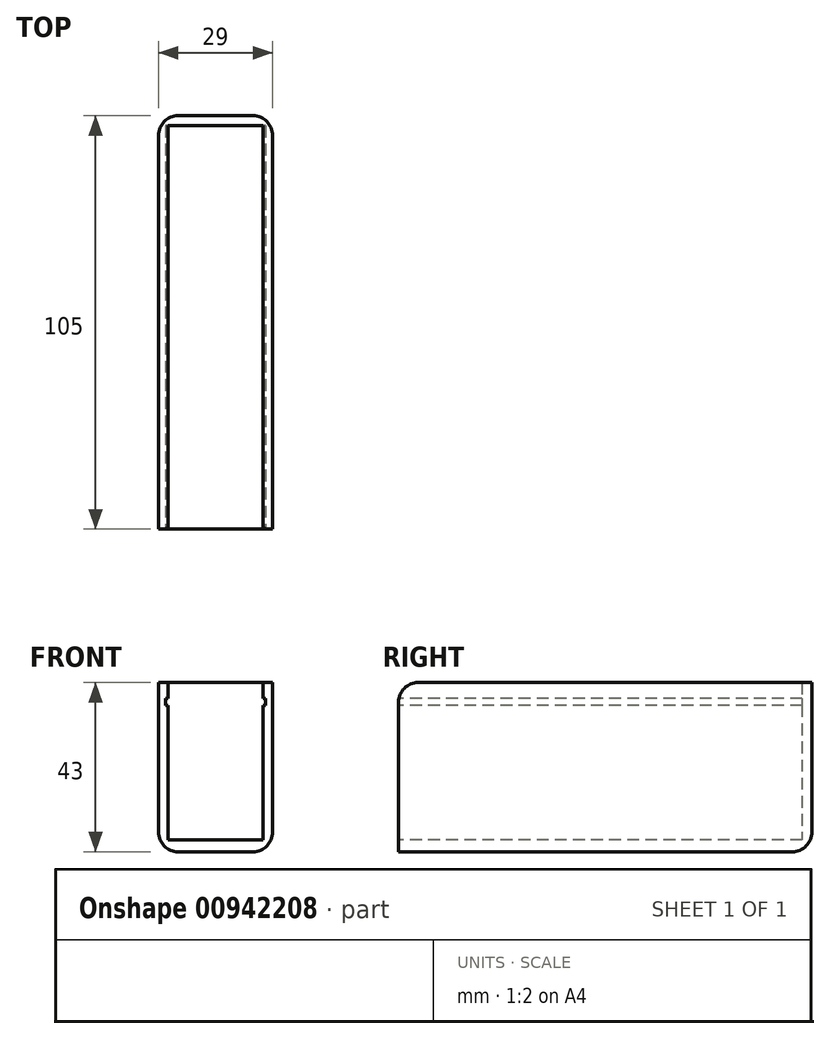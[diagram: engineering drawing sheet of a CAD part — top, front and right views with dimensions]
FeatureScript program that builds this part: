
annotation { "Feature Type Name" : "Feature", "Feature Type Description" : "" }
export const myFeature = defineFeature(function(context is Context, id is Id, definition is map)
    precondition{}
    {
        {
            var Q0;
            Q0=qCreatedBy(makeId("Top.planeOp"),FACE);
            var sketch = newSketch(context, id + "F0", { "sketchPlane" : qUnion([Q0])});
            skLineSegment(sketch, "E0.bottom", {"start": v(12, -50) * mm, "end": v(-12, -50) * mm});
            skLineSegment(sketch, "E0.top", {"start": v(12, 50) * mm, "end": v(-12, 50) * mm});
            skLineSegment(sketch, "E0.left", {"start": v(12, -50) * mm, "end": v(12, 50) * mm});
            skLineSegment(sketch, "E0.right", {"start": v(-12, -50) * mm, "end": v(-12, 50) * mm});
            skPoint(sketch, "E0.middle", {"position": v(0, 0) * mm});
            skLineSegment(sketch, "E1.bottom", {"start": v(14.5, -52.5) * mm, "end": v(-14.5, -52.5) * mm});
            skLineSegment(sketch, "E1.top", {"start": v(14.5, 52.5) * mm, "end": v(-14.5, 52.5) * mm});
            skLineSegment(sketch, "E1.left", {"start": v(14.5, -52.5) * mm, "end": v(14.5, 52.5) * mm});
            skLineSegment(sketch, "E1.right", {"start": v(-14.5, -52.5) * mm, "end": v(-14.5, 52.5) * mm});
            skLineSegment(sketch, "E2", {"start": v(-12, -50) * mm, "end": v(-12, -52.5) * mm});
            skLineSegment(sketch, "E3", {"start": v(12, -50) * mm, "end": v(12, -52.5) * mm});
            skSolve(sketch);
        }
        {
            var Q0;
            Q0=makeQuery(id+"F0.imprint","IMPRINT",FACE,{"disambiguationData":[TD([[makeQuery(id+"F0.imprint","IMPRINT",EDGE,{"derivedFrom":sQuery(id+"F0.wireOp",EDGE,"E0.top")}),-1.0]])]});
            extrude(context, id + "F1", {"entities" : qUnion([Q0]), "depth" : 40 * mm, "offsetDistance" : 25 * mm});
        }
        {
            var Q0;
            Q0=makeQuery(id+"F0.imprint","IMPRINT",FACE,{"disambiguationData":[TD([[makeQuery(id+"F0.imprint","IMPRINT",EDGE,{"derivedFrom":sQuery(id+"F0.wireOp",EDGE,"E0.bottom")}),-1.0]])]});
            var Q1;
            Q1=makeQuery(id+"F0.imprint","IMPRINT",FACE,{"disambiguationData":[TD([[makeQuery(id+"F0.imprint","IMPRINT",EDGE,{"derivedFrom":sQuery(id+"F0.wireOp",EDGE,"E0.top")}),-1.0]])]});
            var Q2;
            Q2=makeQuery(id+"F0.imprint","IMPRINT",FACE,{"disambiguationData":[TD([[makeQuery(id+"F0.imprint","IMPRINT",EDGE,{"derivedFrom":sQuery(id+"F0.wireOp",EDGE,"E0.bottom")}),1.0]])]});
            extrude(context, id + "F2", {"entities" : qUnion([Q0, Q1, Q2]), "operationType" : NewBodyOperationType.ADD, "oppositeDirection" : true, "depth" : 3 * mm, "offsetDistance" : 25 * mm});
        }
        {
            var Q0;
            {var subQ0=sQuery(id+"F0.wireOp",EDGE,"E1.bottom");Q0=makeQuery(id+"F2.boolean.opBoolean","MERGE",FACE,{"derivedFrom":[makeQuery(id+"F1.opExtrude","SWEPT_FACE",FACE,{"disambiguationData":[OSD([subQ0]),TDD([makeQuery(id+"F0.imprint","IMPRINT",EDGE,{"disambiguationData":[TD([[makeQuery(id+"F0.imprint","INTERSECT",VERTEX,{"derivedFrom":[subQ0,sQuery(id+"F0.wireOp",EDGE,"E1.left")]}),-1.0]])],"derivedFrom":subQ0})])]}),makeQuery(id+"F1.opExtrude","SWEPT_FACE",FACE,{"disambiguationData":[OSD([subQ0]),TDD([makeQuery(id+"F0.imprint","IMPRINT",EDGE,{"disambiguationData":[TD([[makeQuery(id+"F0.imprint","INTERSECT",VERTEX,{"derivedFrom":[subQ0,sQuery(id+"F0.wireOp",EDGE,"E1.right")]}),1.0]])],"derivedFrom":subQ0})])]}),makeQuery(id+"F2.opExtrude","SWEPT_FACE",FACE,{"disambiguationData":[OSD([subQ0])]})]});}
            var sketch = newSketch(context, id + "F3", { "sketchPlane" : qUnion([Q0])});
            skLineSegment(sketch, "E4", {"start": v(-12, 36) * mm, "end": v(-12.7, 36) * mm});
            skLineSegment(sketch, "E5", {"start": v(-12.7, 36) * mm, "end": v(-12.7, 34.2) * mm});
            skLineSegment(sketch, "E6", {"start": v(-12.7, 34.2) * mm, "end": v(-12, 34.2) * mm});
            skLineSegment(sketch, "E7.MirrorCS", {"start": v(12.7, 34.2) * mm, "end": v(12, 34.2) * mm});
            skLineSegment(sketch, "E8.MirrorCS", {"start": v(12, 36) * mm, "end": v(12.7, 36) * mm});
            skLineSegment(sketch, "E9.MirrorCS", {"start": v(12.7, 36) * mm, "end": v(12.7, 34.2) * mm});
            skSolve(sketch);
        }
        {
            var Q0;
            {var subQ0=sQuery(id+"F3.wireOp",EDGE,"E4");Q0=makeQuery(id+"F3.imprint","IMPRINT",FACE,{"disambiguationData":[TD([[makeQuery(id+"F3.imprint","IMPRINT",EDGE,{"derivedFrom":subQ0}),1.0]])]});}
            var Q1;
            {var subQ0=sQuery(id+"F3.wireOp",EDGE,"E7.MirrorCS");Q1=makeQuery(id+"F3.imprint","IMPRINT",FACE,{"disambiguationData":[TD([[makeQuery(id+"F3.imprint","IMPRINT",EDGE,{"derivedFrom":subQ0}),-1.0]])]});}
            extrude(context, id + "F4", {"entities" : qUnion([Q0, Q1]), "operationType" : NewBodyOperationType.REMOVE, "oppositeDirection" : true, "depth" : 102.5 * mm, "offsetDistance" : 25 * mm});
        }
        {
            var Q0;
            {var subQ0=sQuery(id+"F0.wireOp",EDGE,"E1.bottom");Q0=makeQuery(id+"F1.opExtrude","CAP_EDGE",EDGE,{"disambiguationData":[OSD([subQ0]),TDD([makeQuery(id+"F0.imprint","IMPRINT",EDGE,{"disambiguationData":[TD([[makeQuery(id+"F0.imprint","INTERSECT",VERTEX,{"derivedFrom":[subQ0,sQuery(id+"F0.wireOp",EDGE,"E1.right")]}),1.0]])],"derivedFrom":subQ0})])],"isStart":false});}
            var Q1;
            {var subQ0=sQuery(id+"F0.wireOp",EDGE,"E1.bottom");Q1=makeQuery(id+"F1.opExtrude","CAP_EDGE",EDGE,{"disambiguationData":[OSD([subQ0]),TDD([makeQuery(id+"F0.imprint","IMPRINT",EDGE,{"disambiguationData":[TD([[makeQuery(id+"F0.imprint","INTERSECT",VERTEX,{"derivedFrom":[subQ0,sQuery(id+"F0.wireOp",EDGE,"E1.left")]}),-1.0]])],"derivedFrom":subQ0})])],"isStart":false});}
            var Q2;
            {var subQ0=sQuery(id+"F0.wireOp",EDGE,"E1.right");var subQ1=sQuery(id+"F0.wireOp",EDGE,"E1.top");Q2=makeQuery(id+"F2.boolean.opBoolean","MERGE",EDGE,{"derivedFrom":[makeQuery(id+"F1.opExtrude","SWEPT_EDGE",EDGE,{"disambiguationData":[OSD([subQ1,subQ0])]}),makeQuery(id+"F2.opExtrude","SWEPT_EDGE",EDGE,{"disambiguationData":[OSD([subQ1,subQ0])]})]});}
            var Q3;
            {var subQ0=sQuery(id+"F0.wireOp",EDGE,"E1.left");var subQ1=sQuery(id+"F0.wireOp",EDGE,"E1.top");Q3=makeQuery(id+"F2.boolean.opBoolean","MERGE",EDGE,{"derivedFrom":[makeQuery(id+"F1.opExtrude","SWEPT_EDGE",EDGE,{"disambiguationData":[OSD([subQ1,subQ0])]}),makeQuery(id+"F2.opExtrude","SWEPT_EDGE",EDGE,{"disambiguationData":[OSD([subQ1,subQ0])]})]});}
            var Q4;
            Q4=makeQuery(id+"F2.opExtrude","CAP_EDGE",EDGE,{"disambiguationData":[OSD([sQuery(id+"F0.wireOp",EDGE,"E1.top")])],"isStart":false});
            var Q5;
            Q5=makeQuery(id+"F2.opExtrude","CAP_EDGE",EDGE,{"disambiguationData":[OSD([sQuery(id+"F0.wireOp",EDGE,"E1.left")])],"isStart":false});
            var Q6;
            Q6=makeQuery(id+"F2.opExtrude","CAP_EDGE",EDGE,{"disambiguationData":[OSD([sQuery(id+"F0.wireOp",EDGE,"E1.right")])],"isStart":false});
            fillet(context, id + "F5", {"entities" : qUnion([Q0, Q1, Q2, Q3, Q4, Q5, Q6]), "radius" : 5 * mm, "tangentPropagation" : true, "allowEdgeOverflow" : false});
        }
    });
